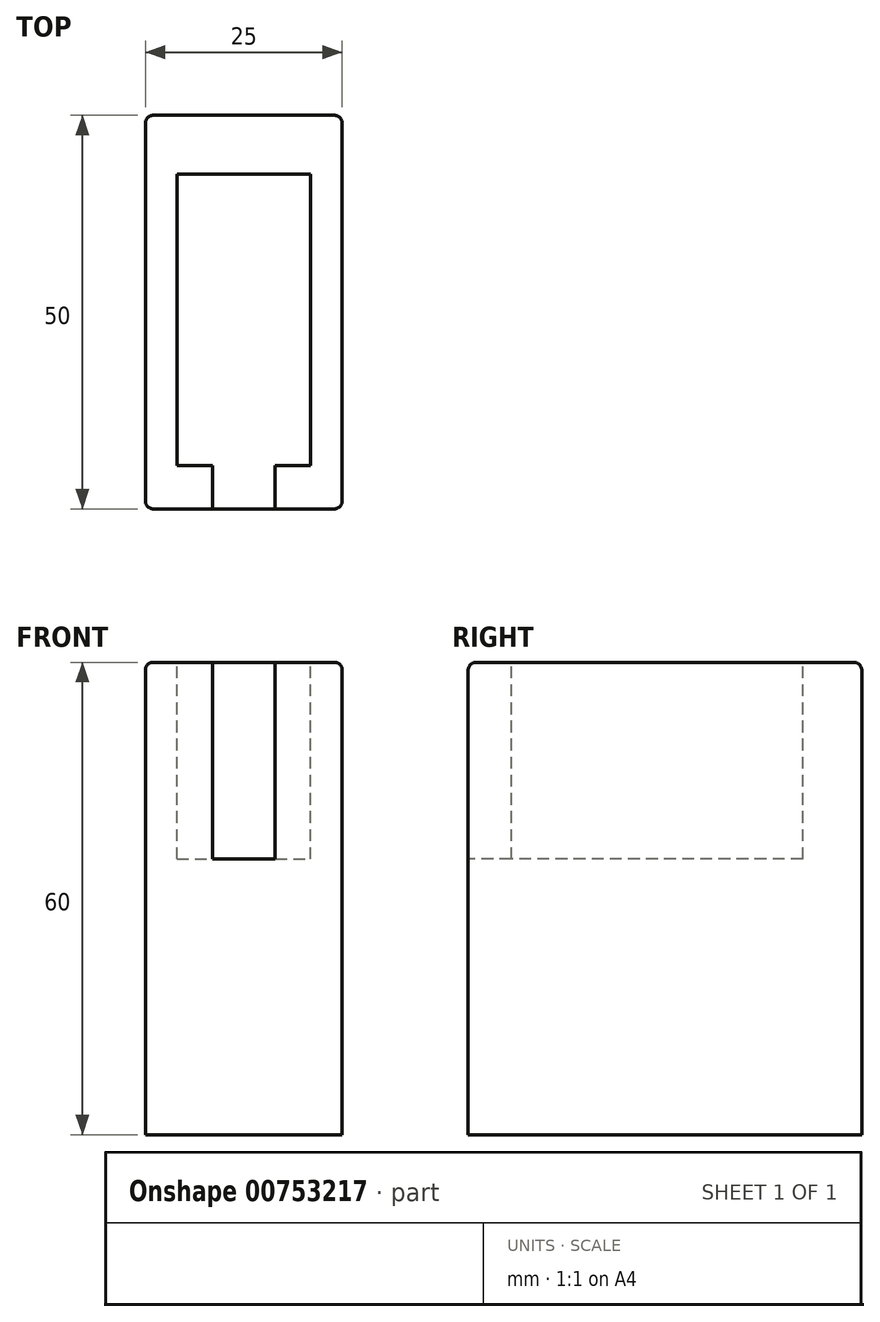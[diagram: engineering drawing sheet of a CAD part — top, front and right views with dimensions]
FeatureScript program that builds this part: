
annotation { "Feature Type Name" : "Feature", "Feature Type Description" : "" }
export const myFeature = defineFeature(function(context is Context, id is Id, definition is map)
    precondition{}
    {
        {
            var Q0;
            Q0=qCreatedBy(makeId("Top.planeOp"),FACE);
            var sketch = newSketch(context, id + "F0", { "sketchPlane" : qUnion([Q0])});
            skLineSegment(sketch, "E0.bottom", {"start": v(0, 0) * mm, "end": v(25, 0) * mm});
            skLineSegment(sketch, "E0.top", {"start": v(0, 50) * mm, "end": v(25, 50) * mm});
            skLineSegment(sketch, "E0.left", {"start": v(0, 0) * mm, "end": v(0, 50) * mm});
            skLineSegment(sketch, "E0.right", {"start": v(25, 0) * mm, "end": v(25, 50) * mm});
            skSolve(sketch);
        }
        {
            var Q0;
            Q0 = qSketchRegion(id + "F0", true);
            extrude(context, id + "F1", {"entities" : qUnion([Q0]), "depth" : 60 * mm, "offsetDistance" : 25 * mm});
        }
        {
            var Q0;
            Q0=makeQuery(id+"F1.opExtrude","CAP_EDGE",EDGE,{"disambiguationData":[OSD([sQuery(id+"F0.wireOp",EDGE,"E0.left")])],"isStart":false});
            var Q1;
            Q1=makeQuery(id+"F1.opExtrude","CAP_EDGE",EDGE,{"disambiguationData":[OSD([sQuery(id+"F0.wireOp",EDGE,"E0.top")])],"isStart":false});
            var Q2;
            Q2=makeQuery(id+"F1.opExtrude","CAP_EDGE",EDGE,{"disambiguationData":[OSD([sQuery(id+"F0.wireOp",EDGE,"E0.right")])],"isStart":false});
            var Q3;
            Q3=makeQuery(id+"F1.opExtrude","SWEPT_EDGE",EDGE,{"disambiguationData":[OSD([sQuery(id+"F0.wireOp",EDGE,"E0.bottom"),sQuery(id+"F0.wireOp",EDGE,"E0.right")])]});
            var Q4;
            Q4=makeQuery(id+"F1.opExtrude","SWEPT_EDGE",EDGE,{"disambiguationData":[OSD([sQuery(id+"F0.wireOp",EDGE,"E0.bottom"),sQuery(id+"F0.wireOp",EDGE,"E0.left")])]});
            var Q5;
            Q5=makeQuery(id+"F1.opExtrude","SWEPT_EDGE",EDGE,{"disambiguationData":[OSD([sQuery(id+"F0.wireOp",EDGE,"E0.top"),sQuery(id+"F0.wireOp",EDGE,"E0.left")])]});
            var Q6;
            Q6=makeQuery(id+"F1.opExtrude","SWEPT_EDGE",EDGE,{"disambiguationData":[OSD([sQuery(id+"F0.wireOp",EDGE,"E0.top"),sQuery(id+"F0.wireOp",EDGE,"E0.right")])]});
            fillet(context, id + "F2", {"entities" : qUnion([Q0, Q1, Q2, Q3, Q4, Q5, Q6]), "tangentPropagation" : true, "radius" : 1 * mm, "defaultsChanged" : false, "vertexSettings" : [], "allowEdgeOverflow" : false});
        }
        {
            var Q0;
            Q0=makeQuery(id+"F1.opExtrude","CAP_FACE",FACE,{"disambiguationData":[OSD([sQuery(id+"F0.wireOp",EDGE,"E0.bottom"),sQuery(id+"F0.wireOp",EDGE,"E0.top"),sQuery(id+"F0.wireOp",EDGE,"E0.left"),sQuery(id+"F0.wireOp",EDGE,"E0.right")])],"isStart":false});
            var sketch = newSketch(context, id + "F3", { "sketchPlane" : qUnion([Q0])});
            skLineSegment(sketch, "E1", {"start": v(1, 49) * mm, "end": v(4, 49) * mm});
            skLineSegment(sketch, "E2", {"start": v(4, 49) * mm, "end": v(4, 42.5) * mm});
            skLineSegment(sketch, "E3", {"start": v(4, 42.5) * mm, "end": v(1, 42.5) * mm});
            skLineSegment(sketch, "E4", {"start": v(4, 42.5) * mm, "end": v(4, 5.5) * mm});
            skLineSegment(sketch, "E5", {"start": v(4, 42.5) * mm, "end": v(21, 42.5) * mm});
            skLineSegment(sketch, "E6", {"start": v(21, 42.5) * mm, "end": v(21, 5.5) * mm});
            skLineSegment(sketch, "E7", {"start": v(21, 5.5) * mm, "end": v(16.5, 5.5) * mm});
            skLineSegment(sketch, "E8", {"start": v(16.5, 5.5) * mm, "end": v(16.5, 0) * mm});
            skLineSegment(sketch, "E9", {"start": v(4, 5.5) * mm, "end": v(8.5, 5.5) * mm});
            skLineSegment(sketch, "E10", {"start": v(8.5, 5.5) * mm, "end": v(8.5, 0) * mm});
            skLineSegment(sketch, "E11", {"start": v(8.5, 0) * mm, "end": v(8.5, -3.06) * mm});
            skLineSegment(sketch, "E12", {"start": v(16.5, 0) * mm, "end": v(16.5, -2.9) * mm});
            skLineSegment(sketch, "E13", {"start": v(8.5, 0) * mm, "end": v(16.5, 0) * mm});
            skSolve(sketch);
        }
        {
            var Q0;
            Q0=makeQuery(id+"F3.imprint","IMPRINT",FACE,{"disambiguationData":[TD([[makeQuery(id+"F3.imprint","IMPRINT",EDGE,{"derivedFrom":sQuery(id+"F3.wireOp",EDGE,"E4")}),1.0]])]});
            extrude(context, id + "F4", {"entities" : qUnion([Q0]), "operationType" : NewBodyOperationType.REMOVE, "oppositeDirection" : true, "depth" : 25 * mm, "offsetDistance" : 25 * mm});
        }
        {
            var Q0;
            {var subQ0=sQuery(id+"F0.wireOp",EDGE,"E0.left");var subQ1=sQuery(id+"F0.wireOp",EDGE,"E0.bottom");Q0=makeQuery(id+"F4.boolean.opBoolean","SPLIT",EDGE,{"disambiguationData":[TD([makeQuery(id+"F2.opFillet","BLEND_FACE",FACE,{"disambiguationData":[OSD([subQ0])]})])],"derivedFrom":makeQuery(id+"F1.opExtrude","CAP_EDGE",EDGE,{"disambiguationData":[OSD([subQ1])],"isStart":false})});}
            var Q1;
            {var subQ0=sQuery(id+"F0.wireOp",EDGE,"E0.right");var subQ1=sQuery(id+"F0.wireOp",EDGE,"E0.bottom");Q1=makeQuery(id+"F4.boolean.opBoolean","SPLIT",EDGE,{"disambiguationData":[TD([makeQuery(id+"F2.opFillet","BLEND_FACE",FACE,{"disambiguationData":[OSD([subQ0])]})])],"derivedFrom":makeQuery(id+"F1.opExtrude","CAP_EDGE",EDGE,{"disambiguationData":[OSD([subQ1])],"isStart":false})});}
            fillet(context, id + "F5", {"entities" : qUnion([Q0, Q1]), "tangentPropagation" : true, "radius" : 1 * mm, "defaultsChanged" : false, "vertexSettings" : [], "allowEdgeOverflow" : false});
        }
    });
